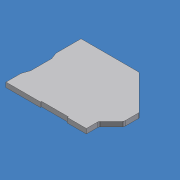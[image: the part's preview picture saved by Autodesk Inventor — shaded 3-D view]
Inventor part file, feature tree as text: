
AUTODESK INVENTOR PART (.ipt)
format: ipt  version: 2012 (Build 160160000, 160)  size: 80,384 bytes
history: native  units: mm (DEFAULTED — no unit token found)
features: extrude x1, sketch x1
ambient origin geometry x8: Origin, YZ Plane, XZ Plane, XY Plane, X Axis, Y Axis, Z Axis, Center Point
bodies: Solid1 (feature_tree)
feature tree (2):
  extrude  "Extrusion1"  [1 undecoded]
  sketch  "Skizze_1"  dims[d0=1.7mm d1=0.0mm]
note: 1 required parameter value undecoded (feature->parameter linkage not recoverable at this tier; creation-order binding heuristic only, values carry confidence <= 0.55)
